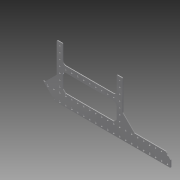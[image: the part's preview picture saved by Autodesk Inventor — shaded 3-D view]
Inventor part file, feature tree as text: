
AUTODESK INVENTOR PART (.ipt)
format: ipt  version: 2014 (Build 180170000, 170)  size: 315,392 bytes
history: native  units: in
note: dims shown in document units (in); Inventor stores cm internally (conversion verified against a paired STEP export)
features: extrude x3, sketch x2
ambient origin geometry x8: Origin, YZ Plane, XZ Plane, XY Plane, X Axis, Y Axis, Z Axis, Center Point
bodies: Solid1 (feature_tree)
feature tree (5):
  extrude  "Extrusion1"  Depth=2.0in
  extrude  "Extrusion2"  Depth=8.0625in
  extrude  "Extrusion3"  TaperAngle=45.0deg  [1 undecoded]
  sketch  "Sketch2"  dims[d0=27.125in d1=2.0in]
  sketch  "Sketch3"  dims[d6=8.0625in d7=8.0625in d8=45.0deg d9=45.0deg d14=135.0deg d15=135.0deg d16=2.0in d17=0.5in d18=7.0in d19=0.5in d20=2.0in d21=0.125in d22=0.125in d23=0.0in d24=1.0in d25=3.0in d26=1.0in d27=1.0in d28=0.5in d29=0.266in d30=0.5in d31=0.5in d32=2.7559in d34=1.0in d35=0.3937in d37=1.0in d39=4.3307in d41=1.0in d42=0.3937in d44=1.0in d46=0.3in d47=0.3125in d48=0.5625in d49=0.7874in d51=1.375in d52=10.6299in d54=1.0in d57=1.0in d58=0.0in d59=0.875in d60=1.0625in d61=1.0in d62=10.2362in d64=1.0in d65=0.3937in d67=1.0in d71=0.25in d72=0.25in d73=1.0in d74=0.0in d75=0.25in d76=0.3in d77=0.25in d78=0.3in]
note: 1 required parameter value undecoded (feature->parameter linkage not recoverable at this tier; creation-order binding heuristic only, values carry confidence <= 0.55)
